# Revit family: Rohrschelle Clipstar, M8, Gummi
name_source: partatom
category: HLS-Bauteile
revit_build: Autodesk Revit 2017 (Build: 20190507_1515(x64)
units: mm (PartAtom-declared; Revit-internal decimal feet)

## family parameters
Arbeitsebenenbasiert = Ja
Beim Laden mit Abzugskörper schneiden = Nein
Bemaßung runder Anschluss = Durchmesser verwenden
Gemeinsam genutzt = Ja
Immer vertikal = Nein
Raumberechnungspunkt = Nein
Teiletyp = Normal

## types (8) — shared parameters
A = 11 mm
Anschluss = M8
Bauart = einteilig
DF1 = 3 mm  [stored 0.00984252 ft]
DS = 3 mm  [stored 0.00984252 ft]
Dämmstärke = 3 mm  [stored 0.00984252 ft]
Fabrikat = MEFA
Farbe Schalldämmeinlage = schwarz
Firma = MEFA Befestigungs- und Montagesysteme GmbH
HGA = 7 mm  [stored 0.0229659 ft]
MD = 1 mm  [stored 0.00328084 ft]
Material = Stahl
Material Schalldämmeinlage = TPE
Materialname = DC01-A
Mengeneinheit = St
Oberflaeche = galvanisch verzinkt
Schalldämmeinlage = Gummi
Verschluss = Hakenverschluss
Vorgabe-Ansicht = 1219 mm
max. Temperaturbeständigkeit = 100 °C
max. zul. Last horizontal = 0.00 kN
max. zul. Last vertikal = 0.00 kN
vpe = 100 St
zero-valued in all types: Nennweite DN Rohr, Stärke Material, max. Rohraußendurchmesser, min. Rohraußendurchmesser

## per-type parameters (varying)
| type | Anschlußhöhe | Artikelnummer | B | Breite | D | D0 | EAN | Gewicht | Gewicht pro Bauteil | H | Höhe | Kurztext1 | Kurztext2 | MB | Materialmaße | R | RM | Rohraußendurchmesser | max. Höhe | max. zul. Last |
| Clipstar, M 8, Ø 10, Gummi | 10 mm | 0290106 | 21 mm | 22 mm  [stored 0.0721785 ft] | 10 mm  [stored 0.0328084 ft] | 16 mm  [stored 0.0524934 ft] | 4250928407559 | 0.01 kg | 0.01 kg | 25 mm  [stored 0.082021 ft] | 26 mm | Rohrschelle Clipstar 16x0,6 | 10 mm M8 TPE | 16 mm  [stored 0.0524934 ft] | 16x0,6 mm | 5 mm  [stored 0.0164042 ft] | 9 mm  [stored 0.0295276 ft] | 10 mm  [stored 0.0328084 ft] | 26 mm | 0.30 kN |
| Clipstar, M 8, Ø 12, Gummi | 10 mm | 0290122 | 23 mm  [stored 0.0754593 ft] | 23 mm  [stored 0.0754593 ft] | 12 mm  [stored 0.0393701 ft] | 18 mm  [stored 0.0590551 ft] | 4250928407566 | 0.01 kg | 0.01 kg | 27 mm | 26 mm | Rohrschelle Clipstar 16x0,6 | 12 mm M8 TPE | 16 mm  [stored 0.0524934 ft] | 16x0,6 mm | 6 mm  [stored 0.019685 ft] | 10 mm  [stored 0.0328084 ft] | 12 mm  [stored 0.0393701 ft] | 26 mm | 0.30 kN |
| Clipstar, M 8, Ø 15, Gummi | 10 mm | 0290157 | 26 mm | 25 mm  [stored 0.082021 ft] | 15 mm  [stored 0.0492126 ft] | 21 mm | 4250928407573 | 0.02 kg | 0.02 kg | 30 mm | 30 mm | Rohrschelle Clipstar 16x0,6 | 15 mm M8 TPE | 16 mm  [stored 0.0524934 ft] | 16x0,6 mm | 8 mm  [stored 0.0262467 ft] | 12 mm  [stored 0.0393701 ft] | 15 mm  [stored 0.0492126 ft] | 30 mm | 0.30 kN |
| Clipstar, M 8, Ø 18, Gummi | 11 mm | 0290181 | 29 mm | 28 mm | 18 mm  [stored 0.0590551 ft] | 24 mm  [stored 0.0787402 ft] | 4250928407580 | 0.02 kg | 0.02 kg | 33 mm | 33 mm | Rohrschelle Clipstar 16x0,6 | 18 mm M8 TPE | 16 mm  [stored 0.0524934 ft] | 16x0,6 mm | 9 mm  [stored 0.0295276 ft] | 13 mm | 18 mm  [stored 0.0590551 ft] | 33 mm | 0.30 kN |
| Clipstar, M 8, Ø 22, Gummi | 11 mm | 0290211 | 33 mm | 31 mm | 22 mm  [stored 0.0721785 ft] | 28 mm | 4250928407597 | 0.02 kg | 0.02 kg | 37 mm | 38 mm | Rohrschelle Clipstar 16x0,8 | 22 mm M8 TPE | 16 mm  [stored 0.0524934 ft] | 16x0,8 mm | 11 mm | 15 mm  [stored 0.0492126 ft] | 22 mm  [stored 0.0721785 ft] | 38 mm | 0.40 kN |
| Clipstar, M 8, Ø 28, Gummi | 11 mm | 0290289 | 39 mm | 39 mm | 28 mm | 34 mm | 4250928407603 | 0.02 kg | 0.02 kg | 43 mm | 44 mm | Rohrschelle Clipstar 16x0,8 | 28 mm M8 TPE | 16 mm  [stored 0.0524934 ft] | 16x0,8 mm | 14 mm  [stored 0.0459318 ft] | 18 mm  [stored 0.0590551 ft] | 28 mm | 44 mm | 0.40 kN |
| Clipstar, M 8, Ø 35, Gummi | 11 mm | 0290351 | 46 mm  [stored 0.150919 ft] | 46 mm  [stored 0.150919 ft] | 35 mm | 41 mm | 4250928407610 | 0.03 kg | 0.03 kg | 50 mm | 51 mm | Rohrschelle Clipstar 20x1,0 | 35 mm M8 TPE | 20 mm  [stored 0.0656168 ft] | 20x1,0 mm | 18 mm  [stored 0.0590551 ft] | 22 mm  [stored 0.0721785 ft] | 35 mm | 51 mm | 0.40 kN |
| Clipstar, M 8, Ø 42, Gummi | 11 mm | 0290424 | 53 mm | 55 mm | 42 mm | 48 mm  [stored 0.15748 ft] | 4250928407627 | 0.04 kg | 0.04 kg | 57 mm | 58 mm | Rohrschelle Clipstar 20x1,0 | 42 mm M8 TPE | 20 mm  [stored 0.0656168 ft] | 20x1,0 mm | 21 mm | 25 mm  [stored 0.082021 ft] | 42 mm | 58 mm | 0.40 kN |

note: [stored X ft] marks values corroborated as IEEE doubles in the binary element streams (Revit-internal decimal feet)

## geometry (parser evidence)
native form markers: Sweep x3
no freeform markers — native parametric forms only
